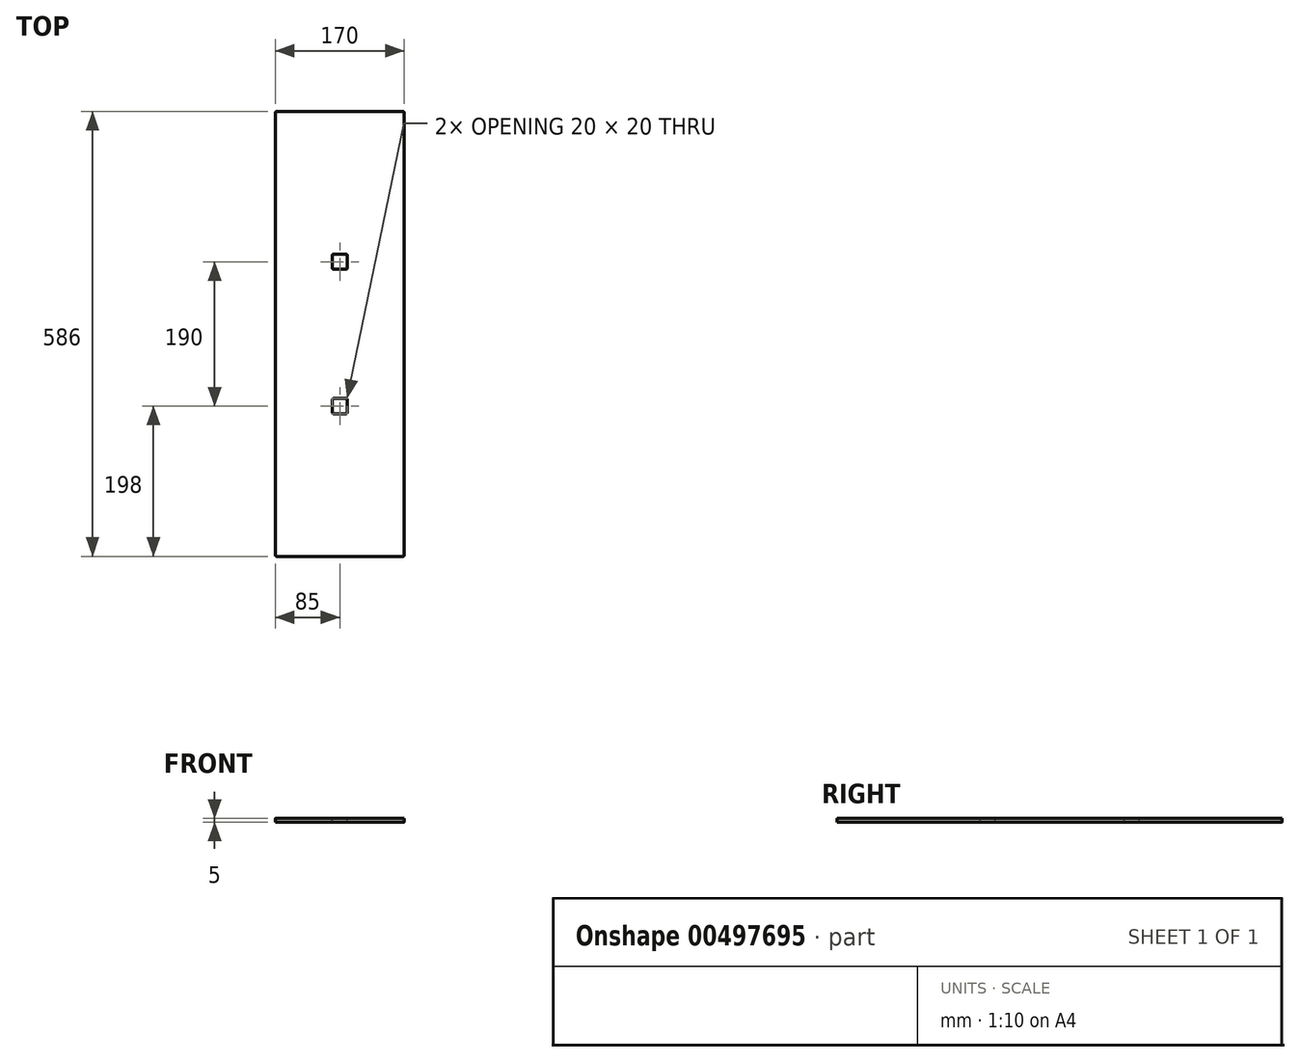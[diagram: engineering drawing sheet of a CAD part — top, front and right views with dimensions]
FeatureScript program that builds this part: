
annotation { "Feature Type Name" : "Feature", "Feature Type Description" : "" }
export const myFeature = defineFeature(function(context is Context, id is Id, definition is map)
    precondition{}
    {
        {
            var Q0;
            Q0=qCreatedBy(makeId("Top.planeOp"),FACE);
            var sketch = newSketch(context, id + "F0", { "sketchPlane" : qUnion([Q0])});
            skLineSegment(sketch, "E0.bottom", {"start": v(-85, 293) * mm, "end": v(85, 293) * mm});
            skLineSegment(sketch, "E0.top", {"start": v(-85, -293) * mm, "end": v(85, -293) * mm});
            skLineSegment(sketch, "E0.left", {"start": v(-85, 293) * mm, "end": v(-85, -293) * mm});
            skLineSegment(sketch, "E0.right", {"start": v(85, 293) * mm, "end": v(85, -293) * mm});
            skPoint(sketch, "E0.middle", {"position": v(0, 0) * mm});
            skSolve(sketch);
        }
        {
            var Q0;
            Q0 = qSketchRegion(id + "F0", true);
            extrude(context, id + "F1", {"entities" : qUnion([Q0]), "depth" : 5 * mm});
        }
        {
            var Q0;
            Q0=makeQuery(id+"F1.opExtrude","CAP_FACE",FACE,{"disambiguationData":[OSD([sQuery(id+"F0.wireOp",EDGE,"E0.bottom"),sQuery(id+"F0.wireOp",EDGE,"E0.top"),sQuery(id+"F0.wireOp",EDGE,"E0.left"),sQuery(id+"F0.wireOp",EDGE,"E0.right")])],"isStart":false});
            var sketch = newSketch(context, id + "F2", { "sketchPlane" : qUnion([Q0])});
            skLineSegment(sketch, "E1", {"start": v(0, 95) * mm, "end": v(0, -95) * mm, "construction": true});
            skLineSegment(sketch, "E2", {"start": v(-27.77, 0) * mm, "end": v(26.14, 0) * mm, "construction": true});
            skLineSegment(sketch, "E3.bottom", {"start": v(10, 85) * mm, "end": v(-10, 85) * mm});
            skLineSegment(sketch, "E3.top", {"start": v(10, 105) * mm, "end": v(-10, 105) * mm});
            skLineSegment(sketch, "E3.left", {"start": v(10, 85) * mm, "end": v(10, 105) * mm});
            skLineSegment(sketch, "E3.right", {"start": v(-10, 85) * mm, "end": v(-10, 105) * mm});
            skPoint(sketch, "E3.middle", {"position": v(0, 95) * mm});
            skLineSegment(sketch, "E4.bottom", {"start": v(10, -105) * mm, "end": v(-10, -105) * mm});
            skLineSegment(sketch, "E4.top", {"start": v(10, -85) * mm, "end": v(-10, -85) * mm});
            skLineSegment(sketch, "E4.left", {"start": v(10, -105) * mm, "end": v(10, -85) * mm});
            skLineSegment(sketch, "E4.right", {"start": v(-10, -105) * mm, "end": v(-10, -85) * mm});
            skPoint(sketch, "E4.middle", {"position": v(0, -95) * mm});
            skSolve(sketch);
        }
        {
            var Q0;
            Q0 = qSketchRegion(id + "F2", true);
            extrude(context, id + "F3", {"entities" : qUnion([Q0]), "operationType" : NewBodyOperationType.REMOVE, "oppositeDirection" : true, "depth" : 25 * mm});
        }
        {
            var Q0;
            Q0=makeQuery(id+"F1.opExtrude","SWEPT_EDGE",EDGE,{"disambiguationData":[OSD([sQuery(id+"F0.wireOp",EDGE,"E0.top"),sQuery(id+"F0.wireOp",EDGE,"E0.left")])]});
            var Q1;
            Q1=makeQuery(id+"F1.opExtrude","SWEPT_EDGE",EDGE,{"disambiguationData":[OSD([sQuery(id+"F0.wireOp",EDGE,"E0.top"),sQuery(id+"F0.wireOp",EDGE,"E0.right")])]});
            var Q2;
            Q2=makeQuery(id+"F1.opExtrude","SWEPT_EDGE",EDGE,{"disambiguationData":[OSD([sQuery(id+"F0.wireOp",EDGE,"E0.bottom"),sQuery(id+"F0.wireOp",EDGE,"E0.right")])]});
            var Q3;
            Q3=makeQuery(id+"F3.boolean.opBoolean","COPY",EDGE,{"derivedFrom":makeQuery(id+"F3.opExtrude","SWEPT_EDGE",EDGE,{"disambiguationData":[OSD([sQuery(id+"F2.wireOp",EDGE,"E3.top"),sQuery(id+"F2.wireOp",EDGE,"E3.right")])]})});
            var Q4;
            Q4=makeQuery(id+"F3.boolean.opBoolean","COPY",EDGE,{"derivedFrom":makeQuery(id+"F3.opExtrude","SWEPT_EDGE",EDGE,{"disambiguationData":[OSD([sQuery(id+"F2.wireOp",EDGE,"E4.top"),sQuery(id+"F2.wireOp",EDGE,"E4.right")])]})});
            var Q5;
            Q5=makeQuery(id+"F3.boolean.opBoolean","COPY",EDGE,{"derivedFrom":makeQuery(id+"F3.opExtrude","SWEPT_EDGE",EDGE,{"disambiguationData":[OSD([sQuery(id+"F2.wireOp",EDGE,"E3.bottom"),sQuery(id+"F2.wireOp",EDGE,"E3.right")])]})});
            var Q6;
            Q6=makeQuery(id+"F3.boolean.opBoolean","COPY",EDGE,{"derivedFrom":makeQuery(id+"F3.opExtrude","SWEPT_EDGE",EDGE,{"disambiguationData":[OSD([sQuery(id+"F2.wireOp",EDGE,"E4.bottom"),sQuery(id+"F2.wireOp",EDGE,"E4.right")])]})});
            var Q7;
            Q7=makeQuery(id+"F3.boolean.opBoolean","COPY",EDGE,{"derivedFrom":makeQuery(id+"F3.opExtrude","SWEPT_EDGE",EDGE,{"disambiguationData":[OSD([sQuery(id+"F2.wireOp",EDGE,"E3.top"),sQuery(id+"F2.wireOp",EDGE,"E3.left")])]})});
            var Q8;
            Q8=makeQuery(id+"F1.opExtrude","SWEPT_EDGE",EDGE,{"disambiguationData":[OSD([sQuery(id+"F0.wireOp",EDGE,"E0.bottom"),sQuery(id+"F0.wireOp",EDGE,"E0.left")])]});
            var Q9;
            Q9=makeQuery(id+"F3.boolean.opBoolean","COPY",EDGE,{"derivedFrom":makeQuery(id+"F3.opExtrude","SWEPT_EDGE",EDGE,{"disambiguationData":[OSD([sQuery(id+"F2.wireOp",EDGE,"E4.top"),sQuery(id+"F2.wireOp",EDGE,"E4.left")])]})});
            var Q10;
            Q10=makeQuery(id+"F3.boolean.opBoolean","COPY",EDGE,{"derivedFrom":makeQuery(id+"F3.opExtrude","SWEPT_EDGE",EDGE,{"disambiguationData":[OSD([sQuery(id+"F2.wireOp",EDGE,"E4.bottom"),sQuery(id+"F2.wireOp",EDGE,"E4.left")])]})});
            var Q11;
            Q11=makeQuery(id+"F3.boolean.opBoolean","COPY",EDGE,{"derivedFrom":makeQuery(id+"F3.opExtrude","SWEPT_EDGE",EDGE,{"disambiguationData":[OSD([sQuery(id+"F2.wireOp",EDGE,"E3.bottom"),sQuery(id+"F2.wireOp",EDGE,"E3.left")])]})});
            fillet(context, id + "F4", {"entities" : qUnion([Q0, Q1, Q2, Q3, Q4, Q5, Q6, Q7, Q8, Q9, Q10, Q11]), "radius" : 2 * mm, "tangentPropagation" : true, "allowEdgeOverflow" : false});
        }
    });
